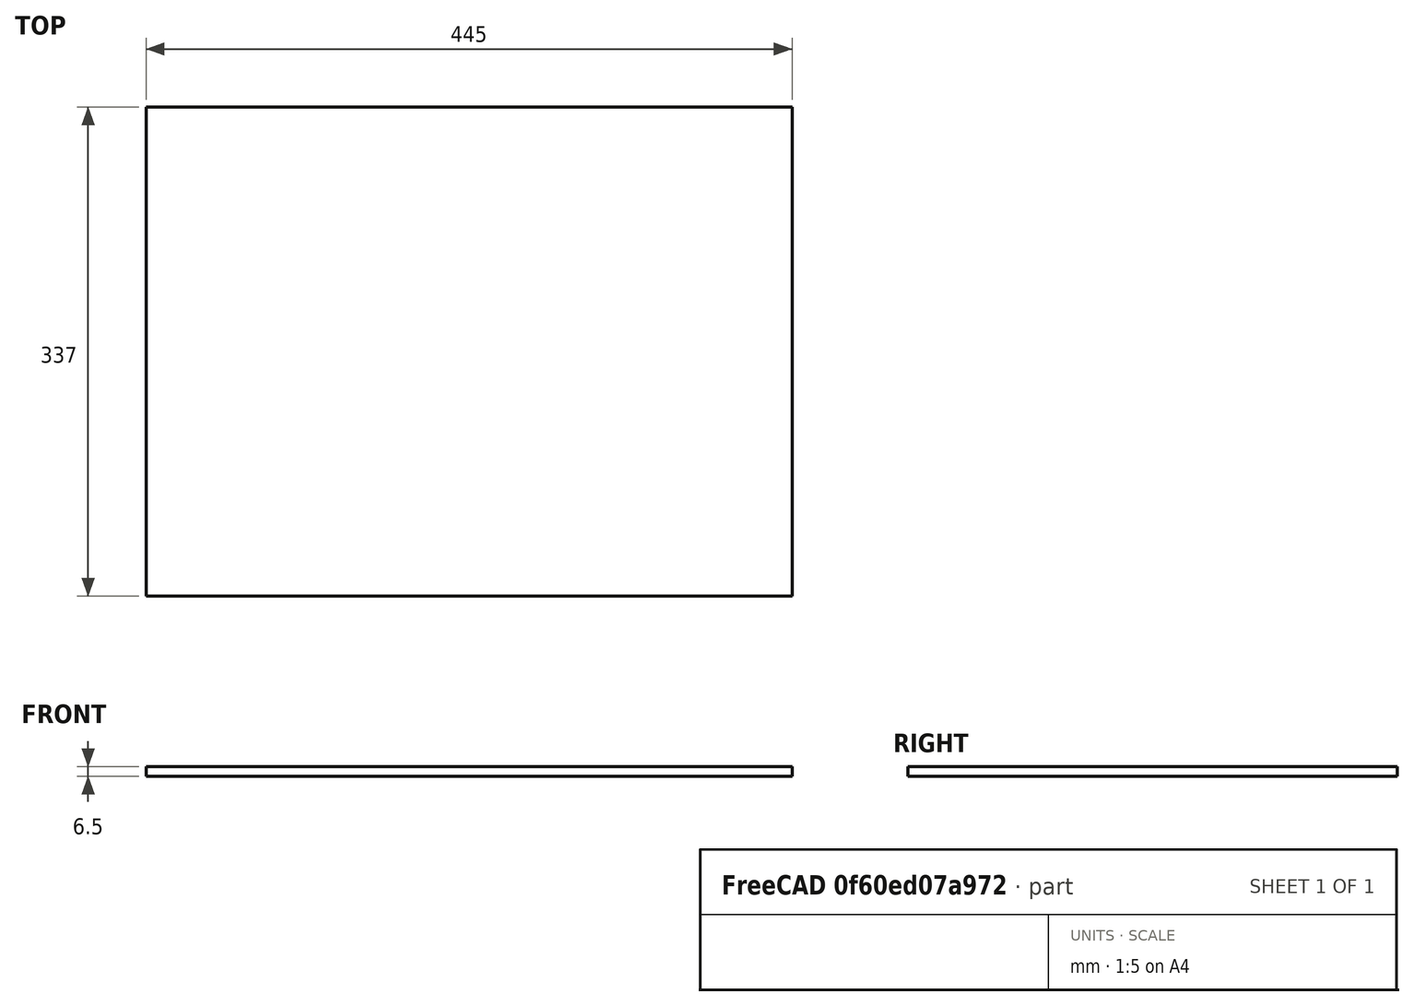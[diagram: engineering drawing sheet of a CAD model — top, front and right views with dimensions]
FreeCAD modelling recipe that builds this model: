
FCSTD DOCUMENT  (FreeCAD 1.0R39109 (Git))
Label: 60_drawer_all_bottom
License: All rights reserved
LicenseURL: http://en.wikipedia.org/wiki/All_rights_reserved
objects: Spreadsheet::Sheet×1, Sketcher::SketchObject×1, PartDesign::Pad×1, PartDesign::Body×1
note: 6 computed .brp shape members not serialized (recipe doc carries the construction recipe); baked Part::Feature solids carry a one-line shape summary decoded from their .brp

FEATURE [Spreadsheet::Sheet] Spreadsheet
  cells = A2='length; B2(length)=445; A3='width; B3(width)=337; A4='height; B4(height)=6.5
FEATURE [Sketcher::SketchObject] Sketch
  ArcFitTolerance = 0
  AttachmentSupport = -> [XY_Plane]
  FullyConstrained = true
  MakeInternals = false
  MapMode = 5
  expr: Constraints[11] = Spreadsheet.length
  expr: Constraints[12] = Spreadsheet.width
  sketch-geometry (5):
    g0: LineSegment StartX=-222.5 StartY=168.5 StartZ=0 EndX=222.5 EndY=168.5 EndZ=0
    g1: LineSegment StartX=222.5 StartY=168.5 StartZ=0 EndX=222.5 EndY=-168.5 EndZ=0
    g2: LineSegment StartX=222.5 StartY=-168.5 StartZ=0 EndX=-222.5 EndY=-168.5 EndZ=0
    g3: LineSegment StartX=-222.5 StartY=-168.5 StartZ=0 EndX=-222.5 EndY=168.5 EndZ=0
    g4: LineSegment [constr] StartX=-222.5 StartY=168.5 StartZ=0 EndX=222.5 EndY=-168.5 EndZ=0
  constraints (13):
    c: Coincident(g0,g1)
    c: Coincident(g1,g2)
    c: Coincident(g2,g3)
    c: Coincident(g3,g0)
    c: Horizontal(g0)
    c: Horizontal(g2)
    c: Vertical(g1)
    c: Vertical(g3)
    c: Coincident(g4,g1)
    c: Coincident(g0,g4)
    c: Symmetric(g0,g1,g-1)
    c: Distance(g0,g0) = 445
    c: Distance(g0,g2) = 337
FEATURE [PartDesign::Pad] Pad
  Direction = (0,0,1)
  Length = 6.5
  Length2 = 10
  Profile = -> Sketch
  ReferenceAxis = -> Sketch [N_Axis]
  Suppressed = false
  Type = 0
  expr: Length = Spreadsheet.height
FEATURE [PartDesign::Body] Body
  AllowCompound = false
  Group = -> [Sketch,Pad]
  Origin = -> Origin
  Tip = -> Pad
